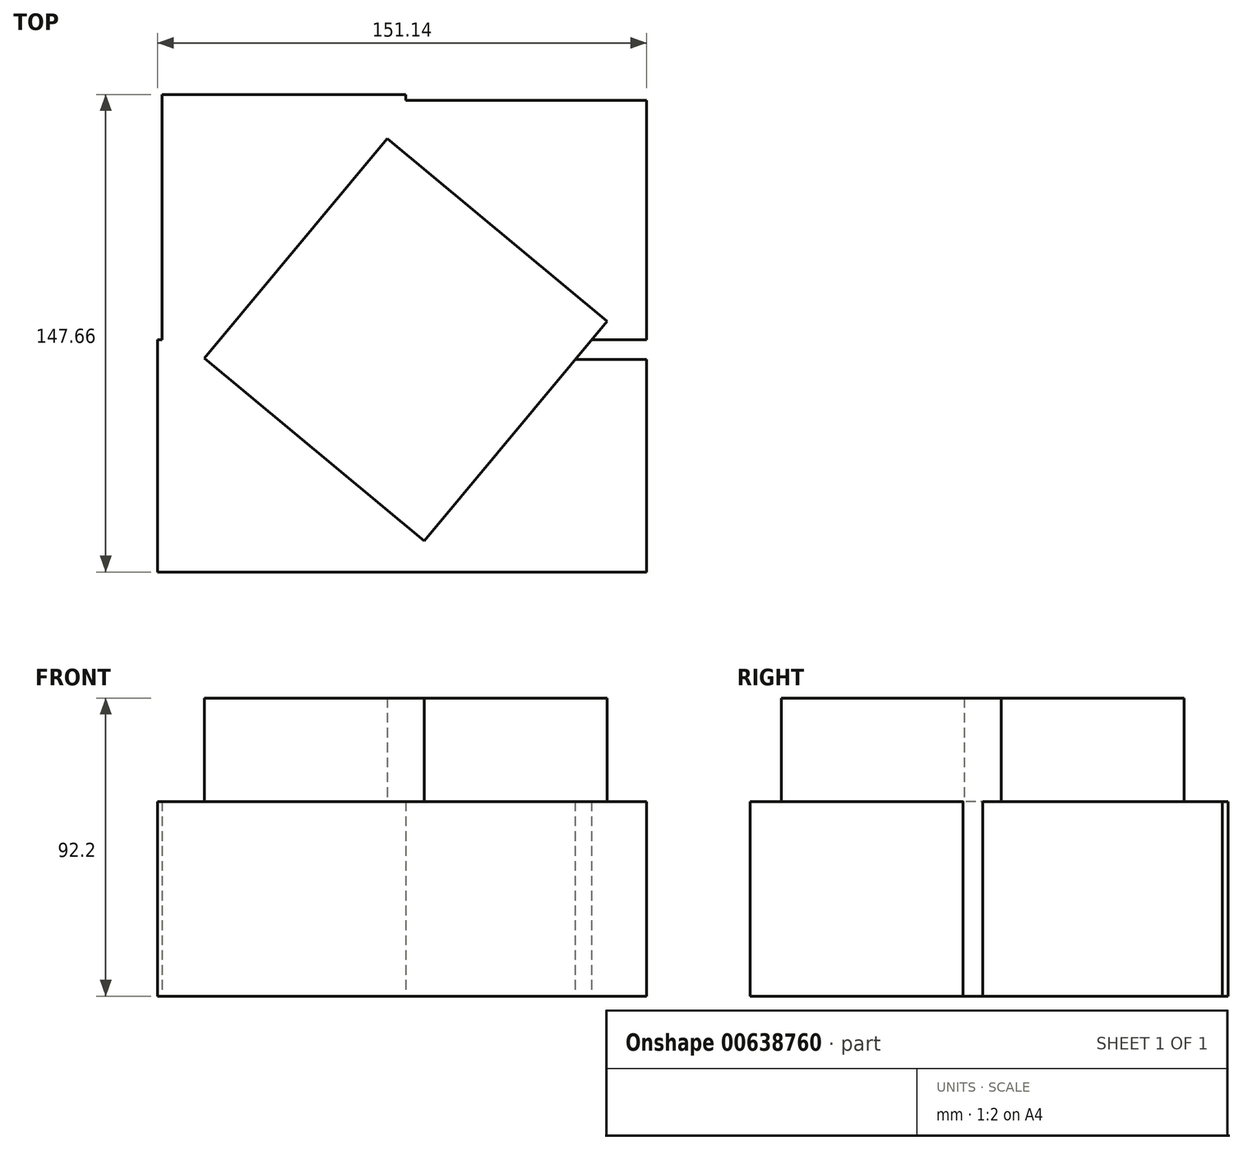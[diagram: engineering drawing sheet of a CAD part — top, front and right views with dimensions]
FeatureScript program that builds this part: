
annotation { "Feature Type Name" : "Feature", "Feature Type Description" : "" }
export const myFeature = defineFeature(function(context is Context, id is Id, definition is map)
    precondition{}
    {
        {
            var Q0;
            Q0=qCreatedBy(makeId("Top.planeOp"),FACE);
            var sketch = newSketch(context, id + "F0", { "sketchPlane" : qUnion([Q0])});
            skLineSegment(sketch, "E0.bottom", {"start": v(0, 0) * mm, "end": v(-75.24, 0) * mm});
            skLineSegment(sketch, "E0.top", {"start": v(0, 75.82) * mm, "end": v(-75.24, 75.82) * mm});
            skLineSegment(sketch, "E0.left", {"start": v(0, 0) * mm, "end": v(0, 75.82) * mm});
            skLineSegment(sketch, "E0.right", {"start": v(-75.24, 0) * mm, "end": v(-75.24, 75.82) * mm});
            skLineSegment(sketch, "E1.bottom", {"start": v(0, -6.12) * mm, "end": v(74.46, -6.12) * mm});
            skLineSegment(sketch, "E1.top", {"start": v(0, -71.84) * mm, "end": v(74.46, -71.84) * mm});
            skLineSegment(sketch, "E1.left", {"start": v(0, -6.12) * mm, "end": v(0, -71.84) * mm});
            skLineSegment(sketch, "E1.right", {"start": v(74.46, -6.12) * mm, "end": v(74.46, -71.84) * mm});
            skLineSegment(sketch, "E2.bottom", {"start": v(0, 0) * mm, "end": v(74.46, 0) * mm});
            skLineSegment(sketch, "E2.top", {"start": v(0, 74.03) * mm, "end": v(74.46, 74.03) * mm});
            skLineSegment(sketch, "E2.left", {"start": v(0, 0) * mm, "end": v(0, 74.03) * mm});
            skLineSegment(sketch, "E2.right", {"start": v(74.46, 0) * mm, "end": v(74.46, 74.03) * mm});
            skLineSegment(sketch, "E3.bottom", {"start": v(0, 0) * mm, "end": v(-76.68, 0) * mm});
            skLineSegment(sketch, "E3.top", {"start": v(0, -71.84) * mm, "end": v(-76.68, -71.84) * mm});
            skLineSegment(sketch, "E3.left", {"start": v(0, 0) * mm, "end": v(0, -71.84) * mm});
            skLineSegment(sketch, "E3.right", {"start": v(-76.68, 0) * mm, "end": v(-76.68, -71.84) * mm});
            skLineSegment(sketch, "E4.bottom", {"start": v(-76.68, -71.84) * mm, "end": v(0, -71.84) * mm});
            skLineSegment(sketch, "E4.top", {"start": v(-76.68, -71.84) * mm, "end": v(0, -71.84) * mm});
            skLineSegment(sketch, "E4.left", {"start": v(-76.68, -71.84) * mm, "end": v(-76.68, -71.84) * mm});
            skLineSegment(sketch, "E4.right", {"start": v(0, -71.84) * mm, "end": v(0, -71.84) * mm});
            skSolve(sketch);
        }
        {
            var Q0;
            {var subQ0=sQuery(id+"F0.wireOp",EDGE,"E1.bottom");Q0=makeQuery(id+"F0.imprint","IMPRINT",FACE,{"disambiguationData":[TD([[makeQuery(id+"F0.imprint","IMPRINT",EDGE,{"derivedFrom":subQ0}),-1.0]])]});}
            var Q1;
            Q1=makeQuery(id+"F0.imprint","IMPRINT",FACE,{"disambiguationData":[TD([[makeQuery(id+"F0.imprint","IMPRINT",EDGE,{"derivedFrom":sQuery(id+"F0.wireOp",EDGE,"E2.bottom")}),1.0]])]});
            var Q2;
            Q2=makeQuery(id+"F0.imprint","IMPRINT",FACE,{"disambiguationData":[TD([[makeQuery(id+"F0.imprint","IMPRINT",EDGE,{"derivedFrom":sQuery(id+"F0.wireOp",EDGE,"E0.top")}),1.0]])]});
            var Q3;
            {var subQ6=sQuery(id+"F0.wireOp",EDGE,"E3.right");Q3=makeQuery(id+"F0.imprint","IMPRINT",FACE,{"disambiguationData":[TD([[makeQuery(id+"F0.imprint","IMPRINT",EDGE,{"derivedFrom":subQ6}),1.0]])]});}
            extrude(context, id + "F1", {"entities" : qUnion([Q0, Q1, Q2, Q3]), "depth" : 60.2 * mm, "offsetDistance" : 25.4 * mm});
        }
        {
            var Q0;
            Q0=qCreatedBy(makeId("Top.planeOp"),FACE);
            var sketch = newSketch(context, id + "F2", { "sketchPlane" : qUnion([Q0])});
            skCircle(sketch, "E5.cCircle", {"center": v(0, 0) * mm, "radius": 44.18 * mm, "construction": true});
            skLineSegment(sketch, "E5.0", {"start": v(-62.22, -5.75) * mm, "end": v(-5.75, 62.22) * mm});
            skLineSegment(sketch, "E5.1", {"start": v(-5.75, 62.22) * mm, "end": v(62.22, 5.75) * mm});
            skLineSegment(sketch, "E5.2", {"start": v(62.22, 5.75) * mm, "end": v(5.75, -62.22) * mm});
            skLineSegment(sketch, "E5.3", {"start": v(5.75, -62.22) * mm, "end": v(-62.22, -5.75) * mm});
            skPoint(sketch, "E5.0.midPoint", {"position": v(-33.99, 28.23) * mm});
            skSolve(sketch);
        }
        {
            var Q0;
            Q0=makeQuery(id+"F2.imprint","IMPRINT",FACE,{"disambiguationData":[TD([[makeQuery(id+"F2.imprint","IMPRINT",EDGE,{"derivedFrom":sQuery(id+"F2.wireOp",EDGE,"E5.0")}),-1.0]])]});
            extrude(context, id + "F3", {"entities" : qUnion([Q0]), "operationType" : NewBodyOperationType.ADD, "depth" : 92.2 * mm, "offsetDistance" : 25.4 * mm});
        }
    });
